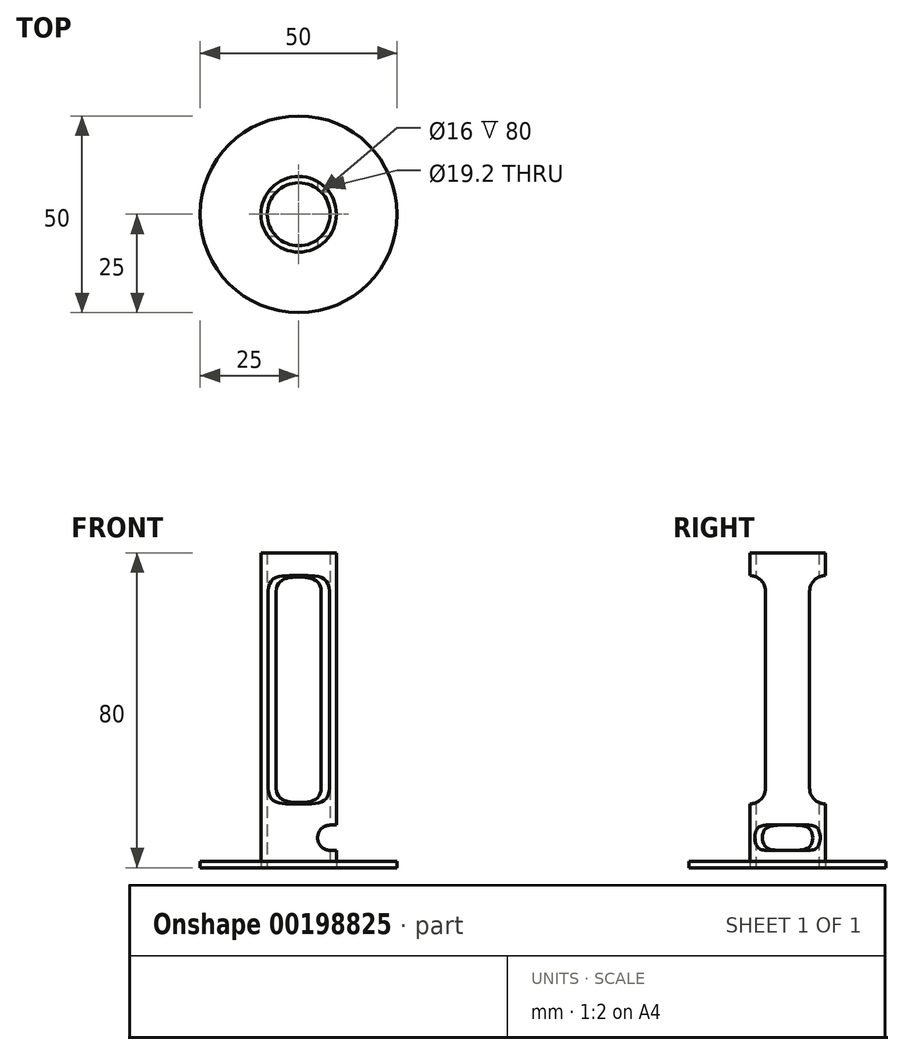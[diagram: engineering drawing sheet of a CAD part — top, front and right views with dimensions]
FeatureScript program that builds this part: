
annotation { "Feature Type Name" : "Feature", "Feature Type Description" : "" }
export const myFeature = defineFeature(function(context is Context, id is Id, definition is map)
    precondition{}
    {
        {
            var Q0;
            Q0=qCreatedBy(makeId("Top.planeOp"),FACE);
            var sketch = newSketch(context, id + "F0", { "sketchPlane" : qUnion([Q0])});
            skCircle(sketch, "E0", {"center": v(0, 0) * mm, "radius": 25 * mm});
            skCircle(sketch, "E1", {"center": v(0, 0) * mm, "radius": 9.6 * mm});
            skCircle(sketch, "E2", {"center": v(0, 0) * mm, "radius": 8 * mm});
            skSolve(sketch);
        }
        {
            var Q0;
            Q0=makeQuery(id+"F0.imprint","IMPRINT",FACE,{"disambiguationData":[TD([[makeQuery(id+"F0.imprint","IMPRINT",EDGE,{"derivedFrom":sQuery(id+"F0.wireOp",EDGE,"E0")}),1.0]])]});
            extrude(context, id + "F1", {"entities" : qUnion([Q0]), "depth" : 1.6 * mm});
        }
        {
            var Q0;
            Q0=makeQuery(id+"F0.imprint","IMPRINT",FACE,{"disambiguationData":[TD([[makeQuery(id+"F0.imprint","IMPRINT",EDGE,{"derivedFrom":sQuery(id+"F0.wireOp",EDGE,"E1")}),1.0]])]});
            var Q1;
            Q1=sQuery(id+"F0.wireOp",EDGE,"E1");
            var Q2;
            Q2=sQuery(id+"F0.wireOp",EDGE,"E2");
            extrude(context, id + "F2", {"entities" : qUnion([Q0]), "surfaceEntities" : qUnion([Q1, Q2]), "depth" : 80 * mm});
        }
        {
            var Q0;
            Q0=qCreatedBy(makeId("Front.planeOp"),FACE);
            var sketch = newSketch(context, id + "F3", { "sketchPlane" : qUnion([Q0])});
            skCircle(sketch, "E3", {"center": v(8, 7.6) * mm, "radius": 3.2 * mm});
            skLineSegment(sketch, "E4.bottom", {"start": v(8, 4.4) * mm, "end": v(18.2, 4.4) * mm});
            skLineSegment(sketch, "E4.top", {"start": v(8, 10.8) * mm, "end": v(18.2, 10.8) * mm});
            skLineSegment(sketch, "E4.left", {"start": v(8, 4.4) * mm, "end": v(8, 10.8) * mm});
            skLineSegment(sketch, "E4.right", {"start": v(18.2, 4.4) * mm, "end": v(18.2, 10.8) * mm});
            skSolve(sketch);
        }
        {
            var Q0;
            Q0=makeQuery(id+"F3.imprint","IMPRINT",FACE,{"disambiguationData":[TD([[makeQuery(id+"F3.imprint","IMPRINT",EDGE,{"derivedFrom":sQuery(id+"F3.wireOp",EDGE,"E3")}),1.0]])]});
            var Q1;
            {var subQ1=sQuery(id+"F3.wireOp",EDGE,"E4.bottom");Q1=makeQuery(id+"F3.imprint","IMPRINT",FACE,{"disambiguationData":[TD([[makeQuery(id+"F3.imprint","IMPRINT",EDGE,{"derivedFrom":subQ1}),1.0]])]});}
            extrude(context, id + "F4", {"entities" : qUnion([Q0, Q1]), "operationType" : NewBodyOperationType.REMOVE, "endBound" : BoundingType.SYMMETRIC, "oppositeDirection" : true, "depth" : 50 * mm});
        }
        {
            var Q0;
            Q0=qCreatedBy(makeId("Right.planeOp"),FACE);
            var sketch = newSketch(context, id + "F5", { "sketchPlane" : qUnion([Q0])});
            skLineSegment(sketch, "E5.bottom", {"start": v(5.6, 70.2) * mm, "end": v(13.6, 70.2) * mm});
            skLineSegment(sketch, "E5.top", {"start": v(5.6, 20.2) * mm, "end": v(13.6, 20.2) * mm});
            skLineSegment(sketch, "E5.left", {"start": v(5.6, 70.2) * mm, "end": v(5.6, 20.2) * mm});
            skLineSegment(sketch, "E5.right", {"start": v(13.6, 70.2) * mm, "end": v(13.6, 20.2) * mm});
            skCircle(sketch, "E6", {"center": v(9.6, 70.2) * mm, "radius": 4 * mm});
            skCircle(sketch, "E7", {"center": v(9.6, 20.2) * mm, "radius": 4 * mm});
            skCircle(sketch, "E8.MirrorC", {"center": v(-9.6, 70.2) * mm, "radius": 4 * mm});
            skLineSegment(sketch, "E9.MirrorCS", {"start": v(-13.6, 70.2) * mm, "end": v(-13.6, 20.2) * mm});
            skLineSegment(sketch, "E10.MirrorCS", {"start": v(-5.6, 70.2) * mm, "end": v(-5.6, 20.2) * mm});
            skCircle(sketch, "E11.MirrorC", {"center": v(-9.6, 20.2) * mm, "radius": 4 * mm});
            skLineSegment(sketch, "E12.MirrorCS", {"start": v(-5.6, 70.2) * mm, "end": v(-13.6, 70.2) * mm});
            skLineSegment(sketch, "E13.MirrorCS", {"start": v(-5.6, 20.2) * mm, "end": v(-13.6, 20.2) * mm});
            skSolve(sketch);
        }
        {
            var Q0;
            {var subQ0=sQuery(id+"F5.wireOp",EDGE,"E5.bottom");Q0=makeQuery(id+"F5.imprint","IMPRINT",FACE,{"disambiguationData":[TD([[makeQuery(id+"F5.imprint","IMPRINT",EDGE,{"derivedFrom":subQ0}),1.0]])]});}
            var Q1;
            {var subQ0=sQuery(id+"F5.wireOp",EDGE,"E5.left");Q1=makeQuery(id+"F5.imprint","IMPRINT",FACE,{"disambiguationData":[TD([[makeQuery(id+"F5.imprint","IMPRINT",EDGE,{"derivedFrom":subQ0}),1.0]])]});}
            var Q2;
            {var subQ0=sQuery(id+"F5.wireOp",EDGE,"E5.top");Q2=makeQuery(id+"F5.imprint","IMPRINT",FACE,{"disambiguationData":[TD([[makeQuery(id+"F5.imprint","IMPRINT",EDGE,{"derivedFrom":subQ0}),-1.0]])]});}
            var Q3;
            {var subQ0=sQuery(id+"F5.wireOp",EDGE,"E5.bottom");Q3=makeQuery(id+"F5.imprint","IMPRINT",FACE,{"disambiguationData":[TD([[makeQuery(id+"F5.imprint","IMPRINT",EDGE,{"derivedFrom":subQ0}),-1.0]])]});}
            var Q4;
            {var subQ0=sQuery(id+"F5.wireOp",EDGE,"E5.top");Q4=makeQuery(id+"F5.imprint","IMPRINT",FACE,{"disambiguationData":[TD([[makeQuery(id+"F5.imprint","IMPRINT",EDGE,{"derivedFrom":subQ0}),1.0]])]});}
            var Q5;
            {var subQ0=sQuery(id+"F5.wireOp",EDGE,"E12.MirrorCS");Q5=makeQuery(id+"F5.imprint","IMPRINT",FACE,{"disambiguationData":[TD([[makeQuery(id+"F5.imprint","IMPRINT",EDGE,{"derivedFrom":subQ0}),-1.0]])]});}
            var Q6;
            {var subQ0=sQuery(id+"F5.wireOp",EDGE,"E12.MirrorCS");Q6=makeQuery(id+"F5.imprint","IMPRINT",FACE,{"disambiguationData":[TD([[makeQuery(id+"F5.imprint","IMPRINT",EDGE,{"derivedFrom":subQ0}),1.0]])]});}
            var Q7;
            {var subQ1=sQuery(id+"F5.wireOp",EDGE,"E9.MirrorCS");Q7=makeQuery(id+"F5.imprint","IMPRINT",FACE,{"disambiguationData":[TD([[makeQuery(id+"F5.imprint","IMPRINT",EDGE,{"derivedFrom":subQ1}),1.0]])]});}
            var Q8;
            {var subQ0=sQuery(id+"F5.wireOp",EDGE,"E13.MirrorCS");Q8=makeQuery(id+"F5.imprint","IMPRINT",FACE,{"disambiguationData":[TD([[makeQuery(id+"F5.imprint","IMPRINT",EDGE,{"derivedFrom":subQ0}),-1.0]])]});}
            var Q9;
            {var subQ0=sQuery(id+"F5.wireOp",EDGE,"E13.MirrorCS");Q9=makeQuery(id+"F5.imprint","IMPRINT",FACE,{"disambiguationData":[TD([[makeQuery(id+"F5.imprint","IMPRINT",EDGE,{"derivedFrom":subQ0}),1.0]])]});}
            extrude(context, id + "F6", {"entities" : qUnion([Q0, Q1, Q2, Q3, Q4, Q5, Q6, Q7, Q8, Q9]), "operationType" : NewBodyOperationType.REMOVE, "endBound" : BoundingType.SYMMETRIC, "depth" : 50 * mm});
        }
    });
